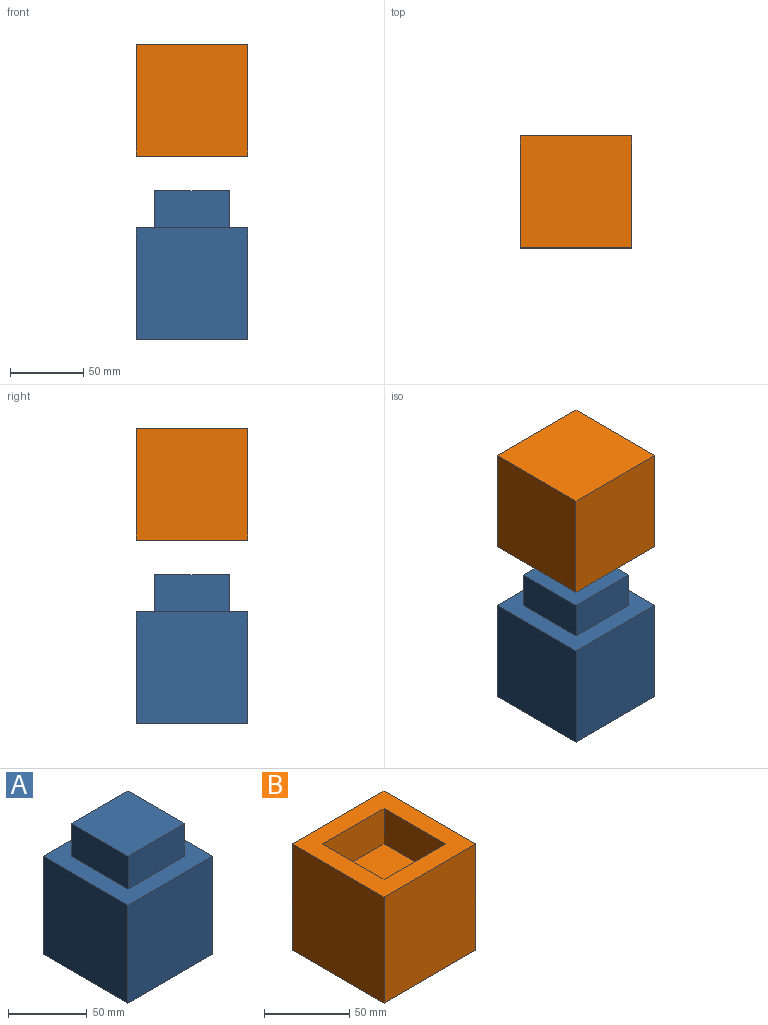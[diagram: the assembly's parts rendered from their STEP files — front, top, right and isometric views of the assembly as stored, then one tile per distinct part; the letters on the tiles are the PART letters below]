
ASSEMBLY  parts=2 mates=2
PART A: 11 faces, bbox 76.2x76.2x101.6 mm
  f0: plane 76.2x76.2mm, normal (0,0,1), area 3225.8mm2, adj f1,f2,f3,f4,f6,f7,f8,f9
  f1: plane 76.2x76.2mm, normal (0,1,0), area 5806.4mm2, adj f0,f2,f4,f5
  f2: plane 76.2x76.2mm, normal (-1,0,0), area 5806.4mm2, adj f0,f1,f3,f5
  f3: plane 76.2x76.2mm, normal (0,-1,0), area 5806.4mm2, adj f0,f2,f4,f5
  f4: plane 76.2x76.2mm, normal (1,0,0), area 5806.4mm2, adj f0,f1,f3,f5
  f5: plane 76.2x76.2mm, normal (0,0,-1), area 5806.4mm2, adj f1,f2,f3,f4
  f6: plane 50.8x25.4mm, normal (0,1,0), area 1290.3mm2, adj f0,f7,f9,f10
  f7: plane 50.8x25.4mm, normal (-1,0,0), area 1290.3mm2, adj f0,f6,f8,f10
  f8: plane 50.8x25.4mm, normal (0,-1,0), area 1290.3mm2, adj f0,f7,f9,f10
  f9: plane 50.8x25.4mm, normal (1,0,0), area 1290.3mm2, adj f0,f6,f8,f10
  f10: plane 50.8x50.8mm, normal (0,0,1), area 2580.6mm2, adj f6,f7,f8,f9
PART B: 11 faces, bbox 76.2x76.2x76.2 mm
  f0: plane 76.2x76.2mm, normal (0,0,1), area 3225.8mm2, adj f1,f2,f3,f4,f6,f7,f8,f9
  f1: plane 76.2x76.2mm, normal (0,1,0), area 5806.4mm2, adj f0,f2,f4,f5
  f2: plane 76.2x76.2mm, normal (-1,0,0), area 5806.4mm2, adj f0,f1,f3,f5
  f3: plane 76.2x76.2mm, normal (0,-1,0), area 5806.4mm2, adj f0,f2,f4,f5
  f4: plane 76.2x76.2mm, normal (1,0,0), area 5806.4mm2, adj f0,f1,f3,f5
  f5: plane 76.2x76.2mm, normal (0,0,-1), area 5806.4mm2, adj f1,f2,f3,f4
  f6: plane 50.8x25.4mm, normal (0,-1,0), area 1290.3mm2, adj f0,f7,f9,f10
  f7: plane 50.8x25.4mm, normal (1,0,0), area 1290.3mm2, adj f0,f6,f8,f10
  f8: plane 50.8x25.4mm, normal (0,1,0), area 1290.3mm2, adj f0,f7,f9,f10
  f9: plane 50.8x25.4mm, normal (-1,0,0), area 1290.3mm2, adj f0,f6,f8,f10
  f10: plane 50.8x50.8mm, normal (0,0,1), area 2580.6mm2, adj f6,f7,f8,f9
PLACE A t=(21.33,28.04,-8.02)mm fixed
PLACE B rot(axis=(1,0,0),180deg) t=(28.77,29.23,193.53)mm
MATE planar B.f4 <-> A.f4  axis (1,0,0) through (67.21,28.01,117.33)mm
MATE planar B.f3 <-> A.f1  axis (0,1,0) through (29.11,66.11,117.33)mm
